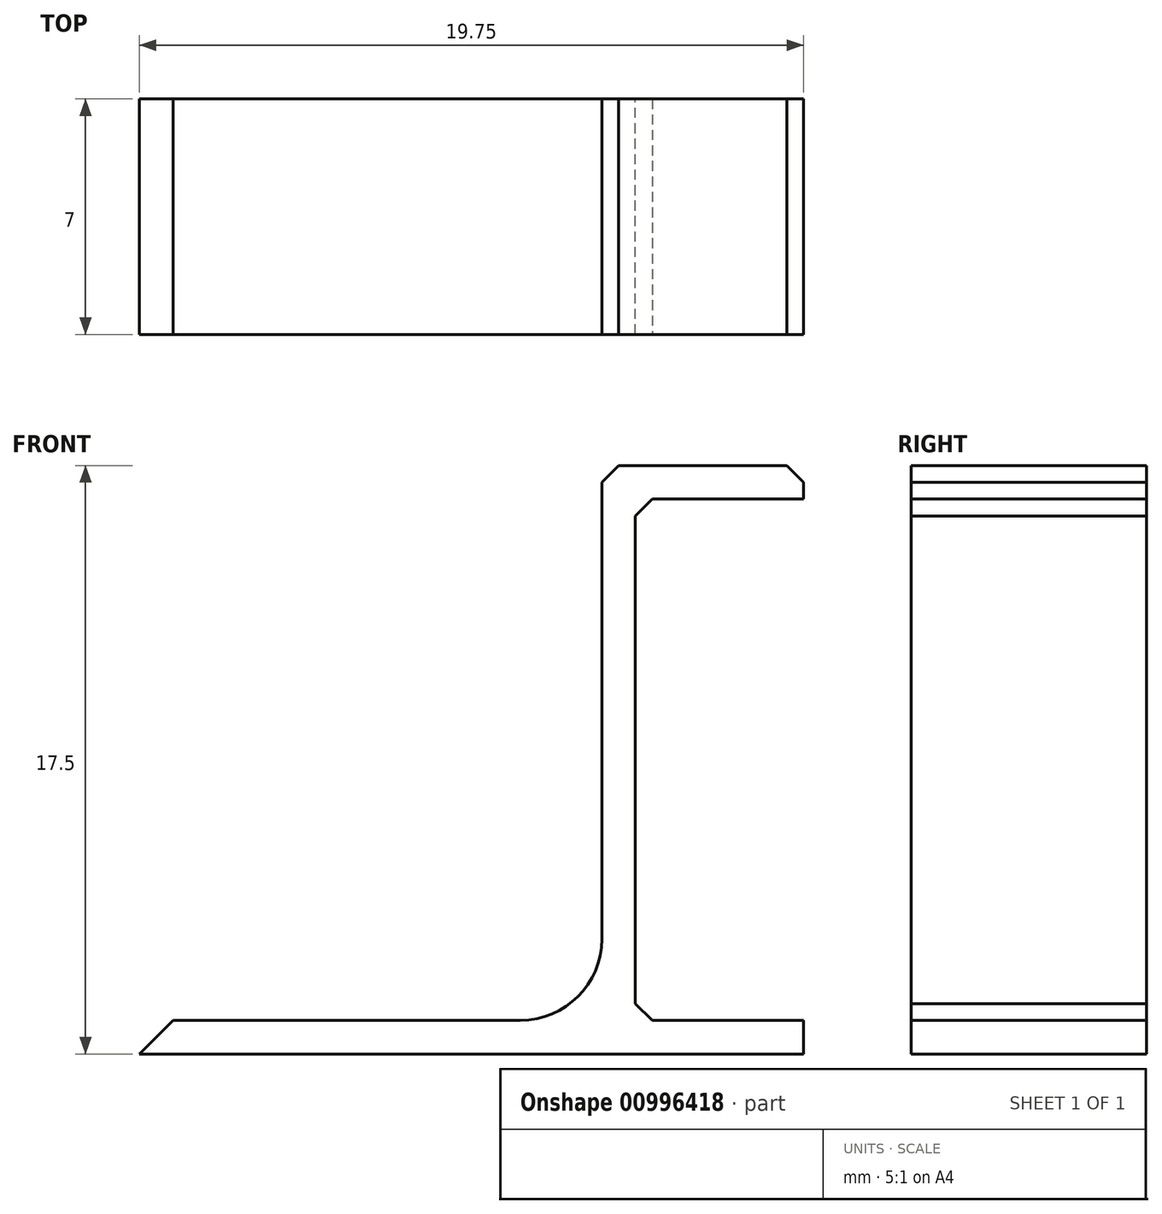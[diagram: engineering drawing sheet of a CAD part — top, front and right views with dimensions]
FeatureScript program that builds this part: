
annotation { "Feature Type Name" : "Feature", "Feature Type Description" : "" }
export const myFeature = defineFeature(function(context is Context, id is Id, definition is map)
    precondition{}
    {
        {
            var Q0;
            Q0=qCreatedBy(makeId("Front.planeOp"),FACE);
            var sketch = newSketch(context, id + "F0", { "sketchPlane" : qUnion([Q0])});
            skLineSegment(sketch, "E0", {"start": v(0, 0) * mm, "end": v(0, 15.5) * mm});
            skLineSegment(sketch, "E1", {"start": v(0, 15.5) * mm, "end": v(5, 15.5) * mm});
            skLineSegment(sketch, "E2", {"start": v(-1, 0) * mm, "end": v(-15, 0) * mm});
            skLineSegment(sketch, "E3", {"start": v(0, 0) * mm, "end": v(5, 0) * mm});
            skLineSegment(sketch, "E4.0", {"start": v(-1, 16.5) * mm, "end": v(5, 16.5) * mm});
            skLineSegment(sketch, "E4.1", {"start": v(-1, 1) * mm, "end": v(-1, 16.5) * mm});
            skLineSegment(sketch, "E5", {"start": v(-15, 0) * mm, "end": v(-15, -1) * mm});
            skLineSegment(sketch, "E6", {"start": v(-15, -1) * mm, "end": v(5, -1) * mm});
            skLineSegment(sketch, "E7", {"start": v(5, -1) * mm, "end": v(5, 0) * mm});
            skLineSegment(sketch, "E8", {"start": v(-1, 1) * mm, "end": v(-1, 0) * mm});
            skLineSegment(sketch, "E9", {"start": v(5, 15.5) * mm, "end": v(5, 16.5) * mm});
            skSolve(sketch);
        }
        {
            var Q0;
            Q0=makeQuery(id+"F0.imprint","IMPRINT",FACE,{"disambiguationData":[TD([[makeQuery(id+"F0.imprint","IMPRINT",EDGE,{"derivedFrom":sQuery(id+"F0.wireOp",EDGE,"E0")}),1.0]])]});
            extrude(context, id + "F1", {"entities" : qUnion([Q0]), "depth" : 7 * mm, "offsetDistance" : 25 * mm});
        }
        {
            var Q0;
            Q0=makeQuery(id+"F1.opExtrude","SWEPT_EDGE",EDGE,{"disambiguationData":[OSD([sQuery(id+"F0.wireOp",EDGE,"E2"),sQuery(id+"F0.wireOp",EDGE,"E8")])]});
            fillet(context, id + "F2", {"entities" : qUnion([Q0]), "radius" : 2.41 * mm, "tangentPropagation" : true, "allowEdgeOverflow" : false});
        }
        {
            var Q0;
            Q0=makeQuery(id+"F1.opExtrude","SWEPT_EDGE",EDGE,{"disambiguationData":[OSD([sQuery(id+"F0.wireOp",EDGE,"E0"),sQuery(id+"F0.wireOp",EDGE,"E3")])]});
            var Q1;
            Q1=makeQuery(id+"F1.opExtrude","SWEPT_EDGE",EDGE,{"disambiguationData":[OSD([sQuery(id+"F0.wireOp",EDGE,"E0"),sQuery(id+"F0.wireOp",EDGE,"E1")])]});
            var Q2;
            Q2=makeQuery(id+"F1.opExtrude","SWEPT_EDGE",EDGE,{"disambiguationData":[OSD([sQuery(id+"F0.wireOp",EDGE,"E4.0"),sQuery(id+"F0.wireOp",EDGE,"E4.1")])]});
            var Q3;
            Q3=makeQuery(id+"F1.opExtrude","SWEPT_EDGE",EDGE,{"disambiguationData":[OSD([sQuery(id+"F0.wireOp",EDGE,"E4.0"),sQuery(id+"F0.wireOp",EDGE,"E9")])]});
            chamfer(context, id + "F3", {"entities" : qUnion([Q0, Q1, Q2, Q3]), "width" : .5 * mm, "tangentPropagation" : true});
        }
        {
            var Q0;
            Q0=makeQuery(id+"F1.opExtrude","SWEPT_EDGE",EDGE,{"disambiguationData":[OSD([sQuery(id+"F0.wireOp",EDGE,"E2"),sQuery(id+"F0.wireOp",EDGE,"E5")])]});
            chamfer(context, id + "F4", {"entities" : qUnion([Q0]), "width" : 1.25 * mm, "tangentPropagation" : true});
        }
    });
